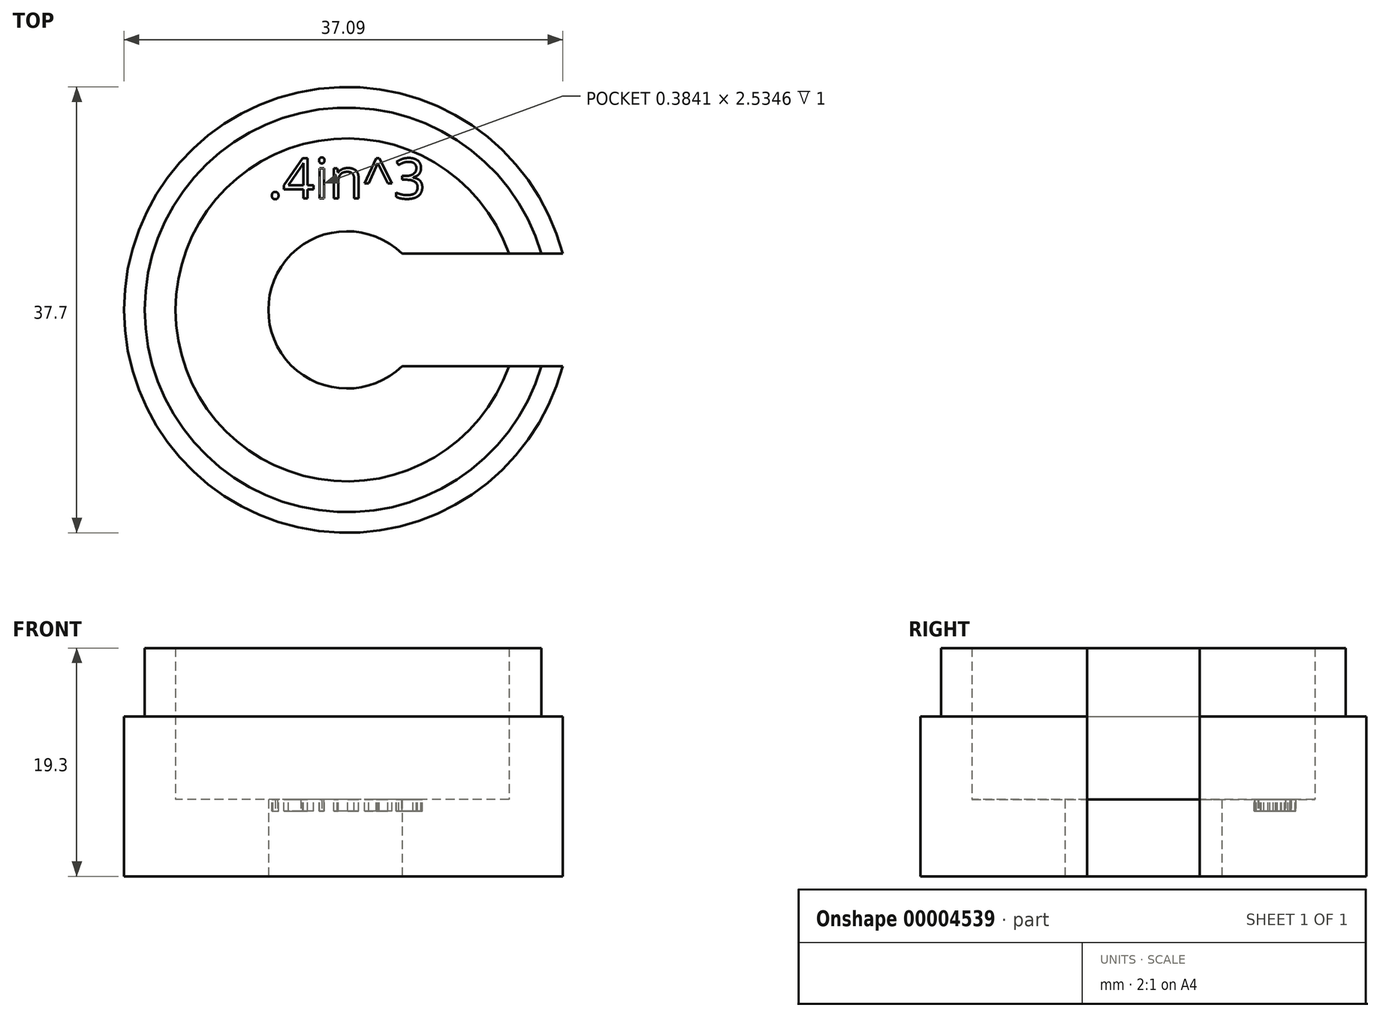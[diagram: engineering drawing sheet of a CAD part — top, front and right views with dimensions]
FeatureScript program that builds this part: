
annotation { "Feature Type Name" : "Feature", "Feature Type Description" : "" }
export const myFeature = defineFeature(function(context is Context, id is Id, definition is map)
    precondition{}
    {
        {
            var Q0;
            Q0=qCreatedBy(makeId("Front.planeOp"),FACE);
            var sketch = newSketch(context, id + "F0", { "sketchPlane" : qUnion([Q0]), "asVersion" : FeatureScriptVersionNumber.V819_ERROR_STRING_ENUM_ASSEMBLY_PATTERN_EXCEED_MAX_INSTANCE_COUNT});
            skLineSegment(sketch, "E0", {"start": v(0, 0) * mm, "end": v(0, 13.5) * mm, "construction": true});
            skLineSegment(sketch, "E1", {"start": v(6.65, 0) * mm, "end": v(18.85, 0) * mm});
            skLineSegment(sketch, "E2", {"start": v(18.85, 0) * mm, "end": v(18.85, 13.5) * mm});
            skLineSegment(sketch, "E3", {"start": v(14.5, 13.5) * mm, "end": v(14.5, 13.5) * mm});
            skLineSegment(sketch, "E4", {"start": v(14.5, 13.5) * mm, "end": v(14.5, 6.5) * mm});
            skLineSegment(sketch, "E5", {"start": v(14.5, 6.5) * mm, "end": v(6.65, 6.5) * mm});
            skLineSegment(sketch, "E6", {"start": v(6.65, 6.5) * mm, "end": v(6.65, 0) * mm});
            skLineSegment(sketch, "E7", {"start": v(14.5, 13.5) * mm, "end": v(14.5, 19.3) * mm});
            skLineSegment(sketch, "E8", {"start": v(14.5, 19.3) * mm, "end": v(17.1, 19.3) * mm});
            skLineSegment(sketch, "E9", {"start": v(17.1, 19.3) * mm, "end": v(17.1, 13.5) * mm});
            skLineSegment(sketch, "E10", {"start": v(17.1, 13.5) * mm, "end": v(18.85, 13.5) * mm});
            skSolve(sketch);
        }
        {
            var Q0;
            Q0 = qSketchRegion(id + "F0", true);
            var Q1;
            Q1=sQuery(id+"F0.wireOp",EDGE,"E0");
            revolve(context, id + "F1", {"entities" : qUnion([Q0]), "axis" : qUnion([Q1]), "revolveType" : RevolveType.FULL});
        }
        {
            var Q0;
            Q0=makeQuery(id+"F1.opRevolve","SWEPT_FACE",FACE,{"disambiguationData":[OSD([sQuery(id+"F0.wireOp",EDGE,"E1")])]});
            var sketch = newSketch(context, id + "F2", { "sketchPlane" : qUnion([Q0]), "asVersion" : FeatureScriptVersionNumber.V819_ERROR_STRING_ENUM_ASSEMBLY_PATTERN_EXCEED_MAX_INSTANCE_COUNT});
            skLineSegment(sketch, "E11", {"start": v(0, 0) * mm, "end": v(18.85, 0) * mm, "construction": true});
            skArc(sketch, "E12.0", {"start": v(4.65, -4.75) * mm, "mid": v(6.65, 0) * mm, "end": v(4.65, 4.75) * mm});
            skArc(sketch, "E13.0", {"start": v(18.24, -4.75) * mm, "mid": v(18.85, 0) * mm, "end": v(18.24, 4.75) * mm});
            skLineSegment(sketch, "E14.bottom", {"start": v(4.65, 4.75) * mm, "end": v(18.24, 4.75) * mm});
            skLineSegment(sketch, "E14.top", {"start": v(4.65, -4.75) * mm, "end": v(18.24, -4.75) * mm});
            skLineSegment(sketch, "E14.left", {"start": v(4.65, 4.75) * mm, "end": v(4.65, -4.75) * mm});
            skSolve(sketch);
        }
        {
            var Q0;
            Q0 = qSketchRegion(id + "F2", true);
            var Q1;
            Q1=makeQuery(id+"F1.opRevolve","SWEPT_FACE",FACE,{"disambiguationData":[OSD([sQuery(id+"F0.wireOp",EDGE,"xKxgd34U-vG4g-Co94-cG5Z-ZDhDzdpa1L3z")])]});
            extrude(context, id + "F3", {"entities" : qUnion([Q0]), "operationType" : NewBodyOperationType.REMOVE, "endBound" : BoundingType.THROUGH_ALL, "oppositeDirection" : true, "endBoundEntityFace" : qUnion([Q1]), "depth" : 25 * mm});
        }
        {
            var Q0;
            Q0=qCreatedBy(makeId("Front.planeOp"),FACE);
            var sketch = newSketch(context, id + "F4", { "sketchPlane" : qUnion([Q0]), "asVersion" : FeatureScriptVersionNumber.V819_ERROR_STRING_ENUM_ASSEMBLY_PATTERN_EXCEED_MAX_INSTANCE_COUNT});
            skLineSegment(sketch, "E15", {"start": v(195.82, -86.97) * mm, "end": v(196.67, -94.28) * mm});
            skLineSegment(sketch, "E16", {"start": v(195.6, -109.62) * mm, "end": v(196.67, -94.28) * mm});
            skLineSegment(sketch, "E17", {"start": v(196.67, -94.28) * mm, "end": v(211.27, -94) * mm});
            skLineSegment(sketch, "E18", {"start": v(167.58, -71.42) * mm, "end": v(235.38, -71.42) * mm});
            skLineSegment(sketch, "E19", {"start": v(63.3, -64.63) * mm, "end": v(65.27, -64.63) * mm});
            skLineSegment(sketch, "E20", {"start": v(45.03, -91.92) * mm, "end": v(44.59, -87.23) * mm});
            skLineSegment(sketch, "E21", {"start": v(29.46, -83.47) * mm, "end": v(29.8, -89.02) * mm});
            skLineSegment(sketch, "E22", {"start": v(62.57, -67.32) * mm, "end": v(58.38, -67.64) * mm});
            skSolve(sketch);
        }
        {
            var Q0;
            Q0=makeQuery(id+"F1.opRevolve","SWEPT_FACE",FACE,{"disambiguationData":[OSD([sQuery(id+"F0.wireOp",EDGE,"E5")])]});
            var sketch = newSketch(context, id + "F5", { "sketchPlane" : qUnion([Q0])});
            skText(sketch, "E23", { "text": ".4in^3", "fontName": "OpenSans-Regular.ttf"});
            skLineSegment(sketch, "E24", {"start": v(0, 7.38) * mm, "end": v(0, 0) * mm, "construction": true});
            const initialGuessF5  = {"E23": [-0.0067, 0.00942, 1, 0, 0.00341]};
            skSetInitialGuess(sketch, initialGuessF5);
            skSolve(sketch);
        }
        {
            var Q0;
            Q0 = qSketchRegion(id + "F5", true);
            extrude(context, id + "F6", {"entities" : qUnion([Q0]), "operationType" : NewBodyOperationType.REMOVE, "flatOperationType" : FlatOperationType.REMOVE, "oppositeDirection" : true, "depth" : 1 * mm, "offsetDistance" : 25 * mm, "domain" : OperationDomain.MODEL});
        }
    });
